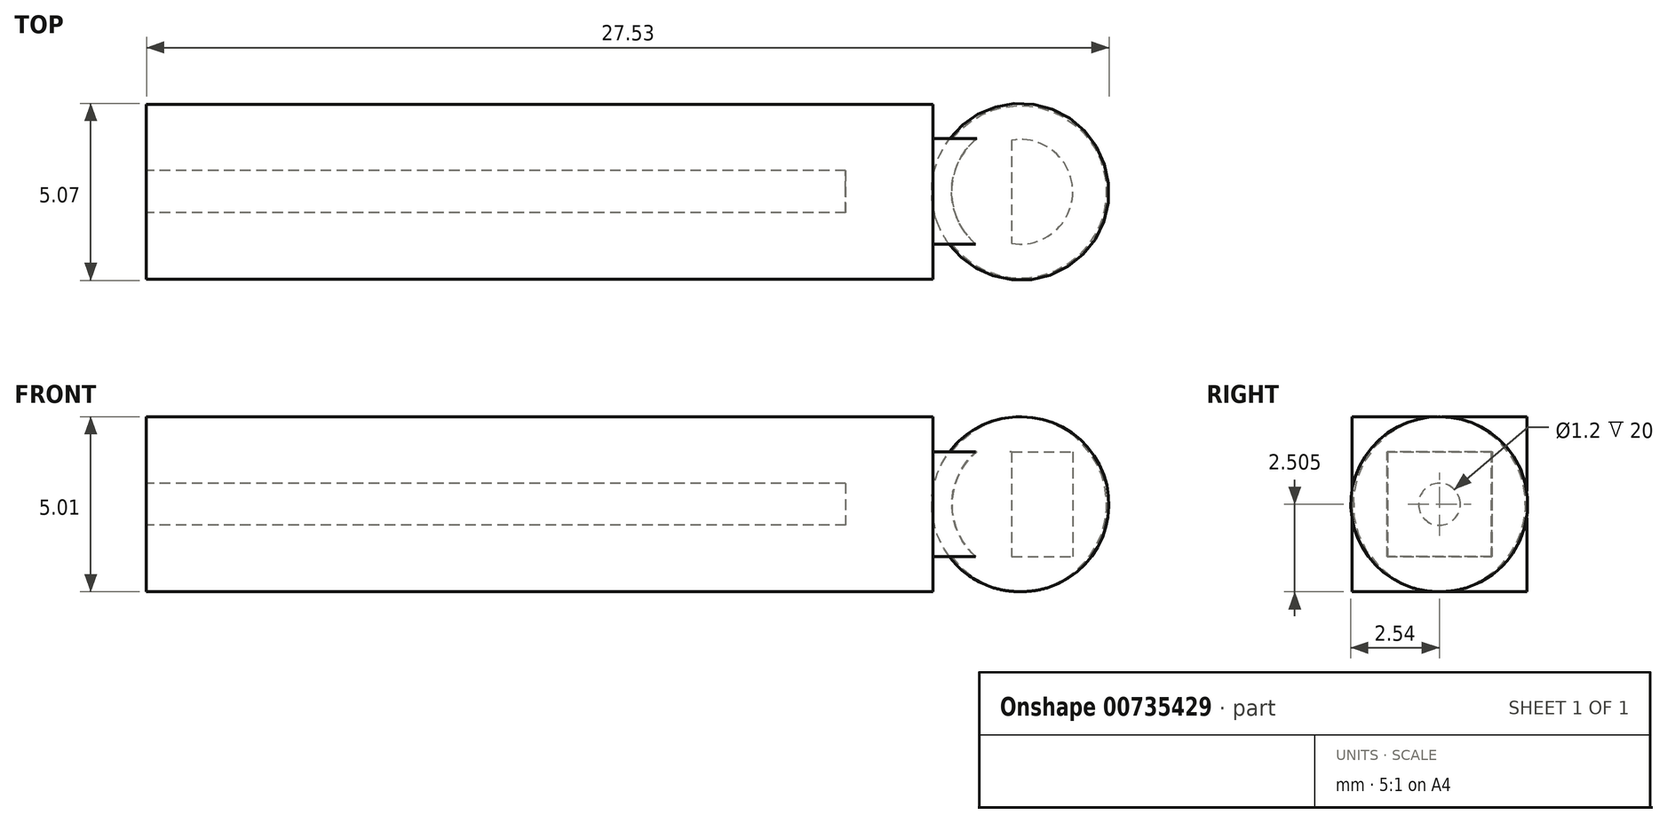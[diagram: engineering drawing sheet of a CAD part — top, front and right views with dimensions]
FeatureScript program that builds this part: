
annotation { "Feature Type Name" : "Feature", "Feature Type Description" : "" }
export const myFeature = defineFeature(function(context is Context, id is Id, definition is map)
    precondition{}
    {
        {
            var Q0;
            Q0=qCreatedBy(makeId("Front.planeOp"),FACE);
            var sketch = newSketch(context, id + "F0", { "sketchPlane" : qUnion([Q0])});
            skLineSegment(sketch, "E0.bottom", {"start": v(-13.65, 28.02) * mm, "end": v(8.85, 28.02) * mm});
            skLineSegment(sketch, "E0.top", {"start": v(-13.65, 23.02) * mm, "end": v(8.85, 23.02) * mm});
            skLineSegment(sketch, "E0.left", {"start": v(-13.65, 28.02) * mm, "end": v(-13.65, 23.02) * mm});
            skLineSegment(sketch, "E0.right", {"start": v(8.85, 28.02) * mm, "end": v(8.85, 23.02) * mm});
            skSolve(sketch);
        }
        {
            var Q0;
            Q0=makeQuery(id+"F0.imprint","IMPRINT",FACE,{"disambiguationData":[TD([[makeQuery(id+"F0.imprint","IMPRINT",EDGE,{"derivedFrom":sQuery(id+"F0.wireOp",EDGE,"E0.bottom")}),-1.0]])]});
            extrude(context, id + "F1", {"entities" : qUnion([Q0]), "depth" : 5 * mm, "offsetDistance" : 25 * mm});
        }
        {
            var Q0;
            Q0=makeQuery(id+"F1.opExtrude","SWEPT_FACE",FACE,{"disambiguationData":[OSD([sQuery(id+"F0.wireOp",EDGE,"E0.left")])]});
            var sketch = newSketch(context, id + "F2", { "sketchPlane" : qUnion([Q0])});
            skCircle(sketch, "E1", {"center": v(2.5, 25.52) * mm, "radius": 0.6 * mm});
            skPoint(sketch, "E1.centerSnap0", {"position": v(5, 25.52) * mm});
            skPoint(sketch, "E1.centerSnap1", {"position": v(2.5, 28.02) * mm});
            skSolve(sketch);
        }
        {
            var Q0;
            Q0=makeQuery(id+"F2.imprint","IMPRINT",FACE,{"disambiguationData":[TD([[makeQuery(id+"F2.imprint","IMPRINT",EDGE,{"derivedFrom":sQuery(id+"F2.wireOp",EDGE,"E1")}),1.0]])]});
            extrude(context, id + "F3", {"entities" : qUnion([Q0]), "operationType" : NewBodyOperationType.REMOVE, "oppositeDirection" : true, "depth" : 20 * mm, "offsetDistance" : 25 * mm});
        }
        {
            var Q0;
            Q0=makeQuery(id+"F1.opExtrude","SWEPT_FACE",FACE,{"disambiguationData":[OSD([sQuery(id+"F0.wireOp",EDGE,"E0.right")])]});
            var sketch = newSketch(context, id + "F4", { "sketchPlane" : qUnion([Q0])});
            skLineSegment(sketch, "E2", {"start": v(-4, 25.52) * mm, "end": v(-4, 27.02) * mm});
            skLineSegment(sketch, "E3", {"start": v(-4, 27.02) * mm, "end": v(-2.5, 27.02) * mm});
            skLineSegment(sketch, "E4", {"start": v(-2.5, 27.02) * mm, "end": v(-0.98, 27.01) * mm});
            skLineSegment(sketch, "E5", {"start": v(-1, 24.02) * mm, "end": v(-4, 24.02) * mm});
            skLineSegment(sketch, "E6", {"start": v(-4, 24.02) * mm, "end": v(-4, 27.02) * mm});
            skLineSegment(sketch, "E7", {"start": v(-1, 24.02) * mm, "end": v(-0.98, 27.01) * mm});
            skSolve(sketch);
        }
        {
            var Q0;
            {var subQ3=sQuery(id+"F4.wireOp",EDGE,"E3");Q0=makeQuery(id+"F4.imprint","IMPRINT",FACE,{"disambiguationData":[TD([[makeQuery(id+"F4.imprint","IMPRINT",EDGE,{"derivedFrom":subQ3}),-1.0]])]});}
            extrude(context, id + "F5", {"entities" : qUnion([Q0]), "operationType" : NewBodyOperationType.ADD, "depth" : 2.5 * mm, "offsetDistance" : 25 * mm});
        }
        {
            var Q0;
            Q0=makeQuery(id+"F5.opExtrude","CAP_FACE",FACE,{"disambiguationData":[OSD([sQuery(id+"F4.wireOp",EDGE,"E3"),sQuery(id+"F4.wireOp",EDGE,"E4"),sQuery(id+"F4.wireOp",EDGE,"E5"),sQuery(id+"F4.wireOp",EDGE,"E6"),sQuery(id+"F4.wireOp",EDGE,"E7")])],"isStart":false});
            var sketch = newSketch(context, id + "F6", { "sketchPlane" : qUnion([Q0])});
            skPoint(sketch, "E8.startSnap0", {"position": v(-2.5, 24.02) * mm});
            skPoint(sketch, "E8.endSnap0", {"position": v(-0.99, 25.51) * mm});
            skArc(sketch, "E9", {"start": v(-2.5, 28.02) * mm, "mid": v(-4.97, 25.51) * mm, "end": v(-2.5, 23.01) * mm});
            skLineSegment(sketch, "E10", {"start": v(-2.5, 23.01) * mm, "end": v(-2.5, 28.02) * mm});
            skSolve(sketch);
        }
        {
            var Q0;
            Q0=makeQuery(id+"F5.opExtrude","CAP_FACE",FACE,{"disambiguationData":[OSD([sQuery(id+"F4.wireOp",EDGE,"E3"),sQuery(id+"F4.wireOp",EDGE,"E4"),sQuery(id+"F4.wireOp",EDGE,"E5"),sQuery(id+"F4.wireOp",EDGE,"E6"),sQuery(id+"F4.wireOp",EDGE,"E7")])],"isStart":false});
            extrude(context, id + "F7", {"entities" : qUnion([Q0]), "operationType" : NewBodyOperationType.REMOVE, "oppositeDirection" : true, "depth" : 0.25 * mm, "offsetDistance" : 25 * mm});
        }
        {
            var Q0;
            {var subQ2=sQuery(id+"F6.wireOp",EDGE,"E9");Q0=makeQuery(id+"F6.imprint","IMPRINT",FACE,{"disambiguationData":[TD([[makeQuery(id+"F6.imprint","IMPRINT",EDGE,{"derivedFrom":subQ2}),1.0]])]});}
            var Q1;
            Q1=sQuery(id+"F6.wireOp",EDGE,"E10");
            revolve(context, id + "F8", {"operationType" : NewBodyOperationType.ADD, "surfaceOperationType" : NewSurfaceOperationType.NEW, "entities" : qUnion([Q0]), "axis" : qUnion([Q1]), "revolveType" : RevolveType.FULL});
        }
    });
